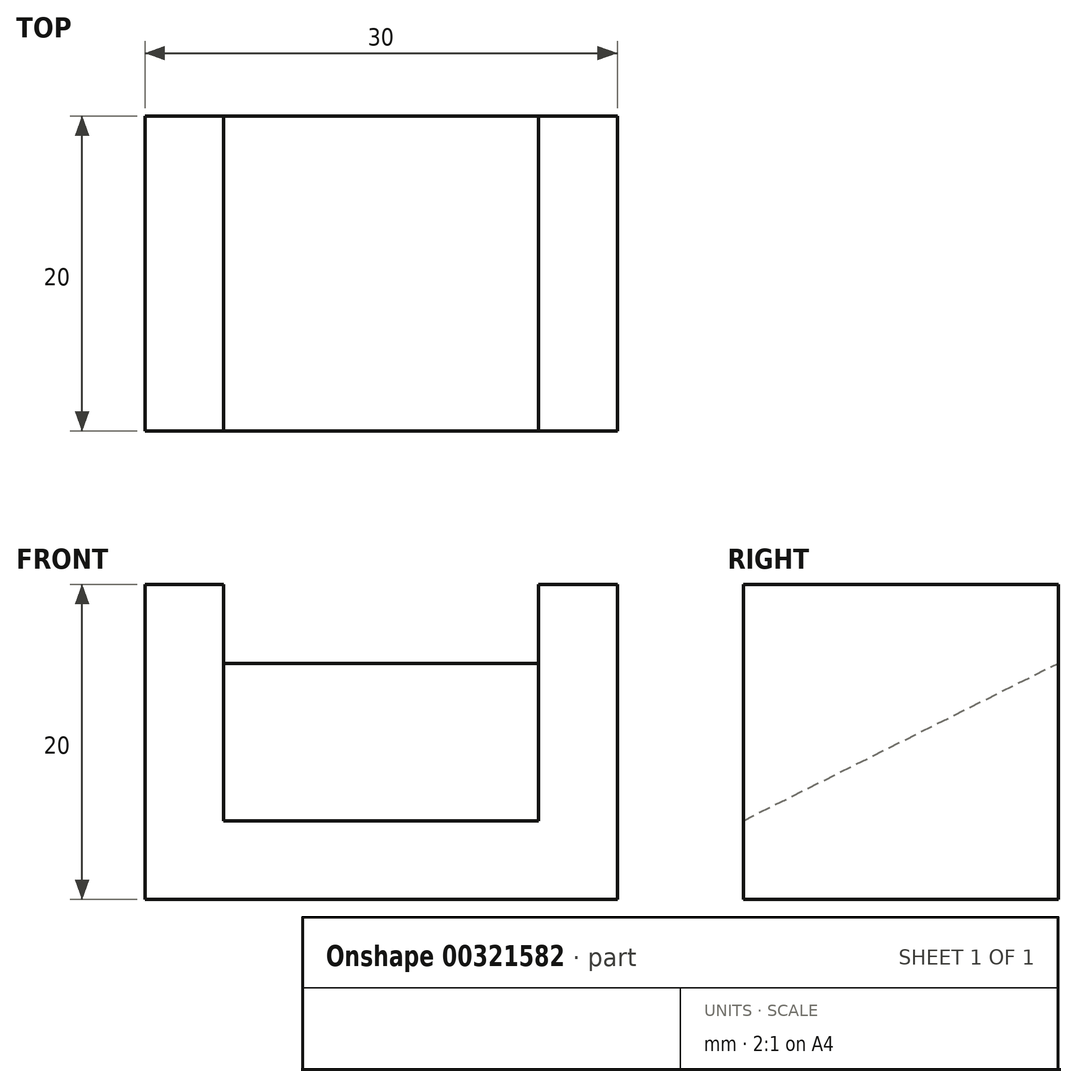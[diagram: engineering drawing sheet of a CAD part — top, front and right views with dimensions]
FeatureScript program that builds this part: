
annotation { "Feature Type Name" : "Feature", "Feature Type Description" : "" }
export const myFeature = defineFeature(function(context is Context, id is Id, definition is map)
    precondition{}
    {
        {
            var Q0;
            Q0=qCreatedBy(makeId("Front.planeOp"),FACE);
            var sketch = newSketch(context, id + "F0", { "sketchPlane" : qUnion([Q0])});
            skLineSegment(sketch, "E0", {"start": v(0, 0) * mm, "end": v(30, 0) * mm});
            skLineSegment(sketch, "E1", {"start": v(30, 0) * mm, "end": v(30, 20) * mm});
            skLineSegment(sketch, "E2", {"start": v(30, 20) * mm, "end": v(0, 20) * mm});
            skLineSegment(sketch, "E3", {"start": v(0, 20) * mm, "end": v(0, 0) * mm});
            skSolve(sketch);
        }
        {
            var Q0;
            Q0=makeQuery(id+"F0.imprint","IMPRINT",FACE,{"disambiguationData":[TD([[makeQuery(id+"F0.imprint","IMPRINT",EDGE,{"derivedFrom":sQuery(id+"F0.wireOp",EDGE,"E0")}),1.0]])]});
            extrude(context, id + "F1", {"entities" : qUnion([Q0]), "depth" : 20 * mm});
        }
        {
            var Q0;
            Q0=makeQuery(id+"F1.opExtrude","SWEPT_FACE",FACE,{"disambiguationData":[OSD([sQuery(id+"F0.wireOp",EDGE,"E1")])]});
            var sketch = newSketch(context, id + "F2", { "sketchPlane" : qUnion([Q0])});
            skLineSegment(sketch, "E4", {"start": v(-20, 5) * mm, "end": v(0, 15) * mm});
            skLineSegment(sketch, "E5", {"start": v(0, 15) * mm, "end": v(0, 20) * mm});
            skLineSegment(sketch, "E6", {"start": v(0, 20) * mm, "end": v(-20, 20) * mm});
            skLineSegment(sketch, "E7", {"start": v(-20, 20) * mm, "end": v(-20, 5) * mm});
            skSolve(sketch);
        }
        {
            var Q0;
            Q0 = qSketchRegion(id + "F2", true);
            extrude(context, id + "F3", {"entities" : qUnion([Q0]), "operationType" : NewBodyOperationType.REMOVE, "oppositeDirection" : true, "depth" : 25 * mm, "hasSecondDirection" : true, "secondDirectionOppositeDirection" : true, "secondDirectionDepth" : 5 * mm});
        }
    });
